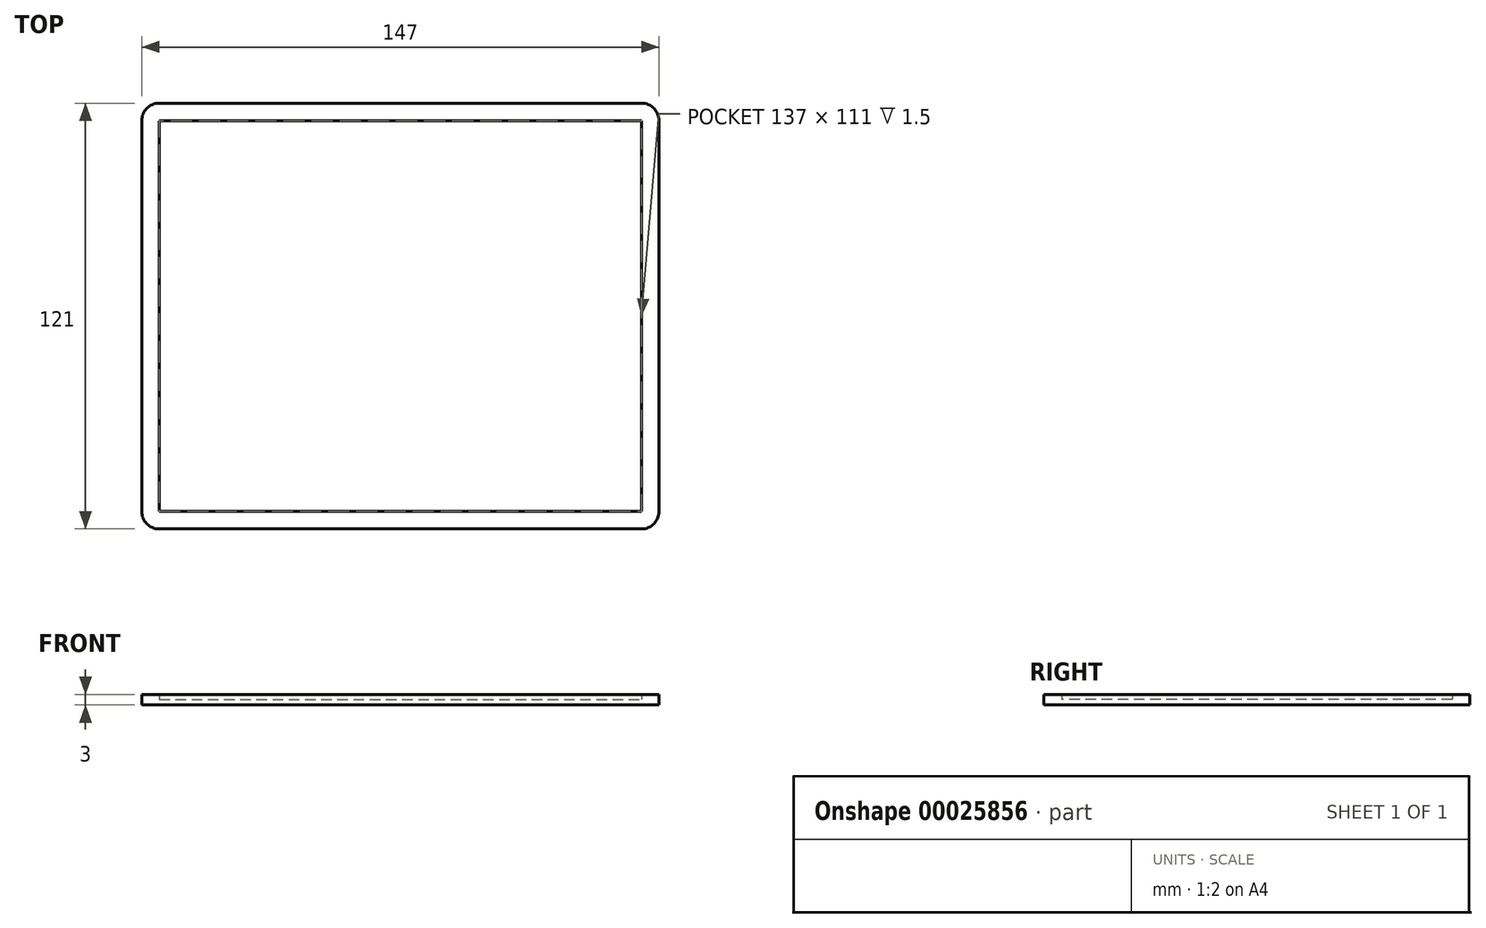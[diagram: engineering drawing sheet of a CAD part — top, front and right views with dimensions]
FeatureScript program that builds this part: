
annotation { "Feature Type Name" : "Feature", "Feature Type Description" : "" }
export const myFeature = defineFeature(function(context is Context, id is Id, definition is map)
    precondition{}
    {
        {
            var Q0;
            Q0=qCreatedBy(makeId("Top.planeOp"),FACE);
            var sketch = newSketch(context, id + "F0", { "sketchPlane" : qUnion([Q0])});
            skLineSegment(sketch, "E0.bottom", {"start": v(-68.5, 55.5) * mm, "end": v(68.5, 55.5) * mm});
            skLineSegment(sketch, "E0.top", {"start": v(-68.5, -55.5) * mm, "end": v(68.5, -55.5) * mm});
            skLineSegment(sketch, "E0.left", {"start": v(-68.5, 55.5) * mm, "end": v(-68.5, -55.5) * mm});
            skLineSegment(sketch, "E0.right", {"start": v(68.5, 55.5) * mm, "end": v(68.5, -55.5) * mm});
            skLineSegment(sketch, "E1.bottom", {"start": v(-73.5, 60.5) * mm, "end": v(73.5, 60.5) * mm});
            skLineSegment(sketch, "E1.top", {"start": v(-73.5, -60.5) * mm, "end": v(73.5, -60.5) * mm});
            skLineSegment(sketch, "E1.left", {"start": v(-73.5, 60.5) * mm, "end": v(-73.5, -60.5) * mm});
            skLineSegment(sketch, "E1.right", {"start": v(73.5, 60.5) * mm, "end": v(73.5, -60.5) * mm});
            skSolve(sketch);
        }
        {
            var Q0;
            Q0=makeQuery(id+"F0.imprint","IMPRINT",FACE,{"disambiguationData":[TD([[makeQuery(id+"F0.imprint","IMPRINT",EDGE,{"derivedFrom":sQuery(id+"F0.wireOp",EDGE,"E0.bottom")}),-1.0]])]});
            extrude(context, id + "F1", {"entities" : qUnion([Q0]), "depth" : 1.5 * mm});
        }
        {
            var Q0;
            Q0=makeQuery(id+"F0.imprint","IMPRINT",FACE,{"disambiguationData":[TD([[makeQuery(id+"F0.imprint","IMPRINT",EDGE,{"derivedFrom":sQuery(id+"F0.wireOp",EDGE,"E0.bottom")}),1.0]])]});
            extrude(context, id + "F2", {"entities" : qUnion([Q0]), "operationType" : NewBodyOperationType.ADD, "depth" : 3 * mm});
        }
        {
            var Q0;
            Q0=makeQuery(id+"F2.opExtrude","SWEPT_EDGE",EDGE,{"disambiguationData":[OSD([sQuery(id+"F0.wireOp",EDGE,"E1.bottom"),sQuery(id+"F0.wireOp",EDGE,"E1.left")])]});
            var Q1;
            Q1=makeQuery(id+"F2.opExtrude","SWEPT_EDGE",EDGE,{"disambiguationData":[OSD([sQuery(id+"F0.wireOp",EDGE,"E1.bottom"),sQuery(id+"F0.wireOp",EDGE,"E1.right")])]});
            var Q2;
            Q2=makeQuery(id+"F2.opExtrude","SWEPT_EDGE",EDGE,{"disambiguationData":[OSD([sQuery(id+"F0.wireOp",EDGE,"E1.top"),sQuery(id+"F0.wireOp",EDGE,"E1.left")])]});
            var Q3;
            Q3=makeQuery(id+"F2.opExtrude","SWEPT_EDGE",EDGE,{"disambiguationData":[OSD([sQuery(id+"F0.wireOp",EDGE,"E1.top"),sQuery(id+"F0.wireOp",EDGE,"E1.right")])]});
            fillet(context, id + "F3", {"entities" : qUnion([Q0, Q1, Q2, Q3]), "radius" : 5 * mm, "tangentPropagation" : true, "allowEdgeOverflow" : false});
        }
    });
